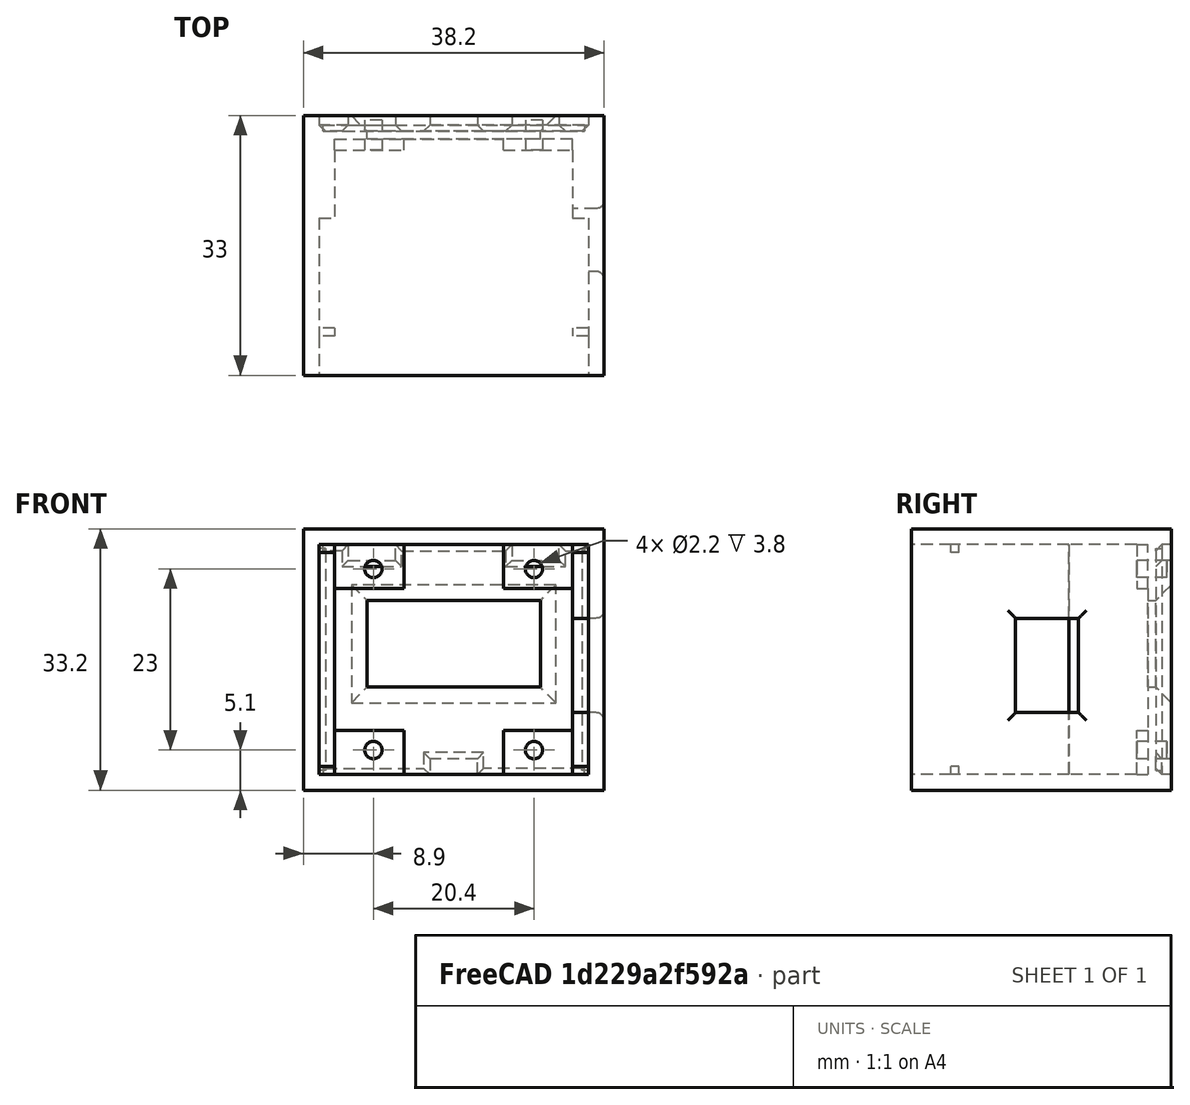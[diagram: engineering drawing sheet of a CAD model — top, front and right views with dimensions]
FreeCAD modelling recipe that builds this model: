
FCSTD DOCUMENT  (FreeCAD 1.2R20251216 (Git shallow))
Label: oled128x64_096-esp8266
License: All rights reserved
LicenseURL: https://en.wikipedia.org/wiki/All_rights_reserved
objects: Sketcher::SketchObject×9, PartDesign::Pad×6, PartDesign::Pocket×3, App::Point×2, PartDesign::Chamfer×2, PartDesign::Body×2, PartDesign::SubShapeBinder×1, PartDesign::Fillet×1
note: 57 computed .brp shape members not serialized (recipe doc carries the construction recipe); baked Part::Feature solids carry a one-line shape summary decoded from their .brp

FEATURE [App::Point] Origin001
  Role = Origin
FEATURE [Sketcher::SketchObject] Sketch  label="base"
  ArcFitTolerance = 1e-06
  AttachmentSupport = -> [Origin]
  ExternalTypes = [0]
  FullyConstrained = true
  MakeInternals = false
  MapMode = 5
  Placement = pos=(0,0,0) rot=(1,0,0;1.5708rad)
  sketch-geometry (5):
    g0: LineSegment StartX=-19.1 StartY=-16.6 StartZ=0 EndX=19.1 EndY=-16.6 EndZ=0
    g1: LineSegment StartX=19.1 StartY=-16.6 StartZ=0 EndX=19.1 EndY=16.6 EndZ=0
    g2: LineSegment StartX=19.1 StartY=16.6 StartZ=0 EndX=-19.1 EndY=16.6 EndZ=0
    g3: LineSegment StartX=-19.1 StartY=16.6 StartZ=0 EndX=-19.1 EndY=-16.6 EndZ=0
    g4: GeomPoint [constr] X=0 Y=0 Z=0
  constraints (12):
    c: Coincident(g0,g1)
    c: Coincident(g1,g2)
    c: Coincident(g2,g3)
    c: Coincident(g3,g0)
    c: Horizontal(g0)
    c: Horizontal(g2)
    c: Vertical(g1)
    c: Vertical(g3)
    c: Symmetric(g2,g0,g4)
    c: Distance(g1,g3) = 38.2
    c: Distance(g0,g2) = 33.2
    c: Coincident(g4,g-1)
FEATURE [PartDesign::Pad] Pad  label="base-pad"
  Direction = (0,-1,2e-16)
  Length = 3
  Length2 = 10
  Profile = -> Sketch
  ReferenceAxis = -> Sketch [N_Axis]
  Refine = true
  SideType = 0
  Suppressed = false
  Type = 0
  Type2 = 0
FEATURE [Sketcher::SketchObject] Sketch001  label="arduino-support-sketch"
  ArcFitTolerance = 1e-06
  AttachmentSupport = -> [Pad]
  ExternalGeometry = -> [Pad]
  ExternalTypes = [0,0,0,0]
  FullyConstrained = true
  MakeInternals = false
  MapMode = 5
  Placement = pos=(0,-3,0) rot=(1,0,0;1.5708rad)
  sketch-geometry (5):
    g0: LineSegment StartX=-15.1 StartY=-14.6 StartZ=0 EndX=15.1 EndY=-14.6 EndZ=0
    g1: LineSegment StartX=15.1 StartY=-14.6 StartZ=0 EndX=15.1 EndY=14.6 EndZ=0
    g2: LineSegment StartX=15.1 StartY=14.6 StartZ=0 EndX=-15.1 EndY=14.6 EndZ=0
    g3: LineSegment StartX=-15.1 StartY=14.6 StartZ=0 EndX=-15.1 EndY=-14.6 EndZ=0
    g4: GeomPoint [constr] X=0 Y=0 Z=0
  constraints (12):
    c: Coincident(g0,g1)
    c: Coincident(g1,g2)
    c: Coincident(g2,g3)
    c: Coincident(g3,g0)
    c: Horizontal(g0)
    c: Horizontal(g2)
    c: Vertical(g1)
    c: Vertical(g3)
    c: Symmetric(g2,g0,g4)
    c: Coincident(g4,g-1)
    c: DistanceY(g2,g-5) = 2
    c: DistanceX(g-4,g0) = 4
FEATURE [PartDesign::Pad] Pad001  label="arduino-support-pad"
  BaseFeature = -> Pad
  Direction = (0,-1,2e-16)
  Length = 10
  Length2 = 10
  Profile = -> Sketch001
  ReferenceAxis = -> Sketch001 [N_Axis]
  Refine = true
  SideType = 0
  Suppressed = false
  Type = 0
  Type2 = 0
FEATURE [Sketcher::SketchObject] Sketch002  label="sides-sketch"
  ArcFitTolerance = 1e-06
  AttachmentSupport = -> [Pad001]
  ExternalGeometry = -> [Pad001]
  ExternalTypes = [0,0,0,0,0]
  FullyConstrained = true
  MakeInternals = false
  MapMode = 5
  Placement = pos=(0,-13,0) rot=(1,0,0;1.5708rad)
  sketch-geometry (7):
    g0: LineSegment StartX=-17.1 StartY=-14.6 StartZ=0 EndX=17.1 EndY=-14.6 EndZ=0
    g1: LineSegment StartX=17.1 StartY=-14.6 StartZ=0 EndX=17.1 EndY=14.6 EndZ=0
    g2: LineSegment StartX=17.1 StartY=14.6 StartZ=0 EndX=-17.1 EndY=14.6 EndZ=0
    g3: LineSegment StartX=-17.1 StartY=14.6 StartZ=0 EndX=-17.1 EndY=-14.6 EndZ=0
    g4: GeomPoint [constr] X=0 Y=0 Z=0
    g5: LineSegment [constr] StartX=1.1e-15 StartY=16.6 StartZ=0 EndX=-2.4e-15 EndY=14.6 EndZ=0
    g6: LineSegment [constr] StartX=-19.1 StartY=1.8e-15 StartZ=0 EndX=-17.1 EndY=1.8e-15 EndZ=0
  constraints (17):
    c: Coincident(g0,g1)
    c: Coincident(g1,g2)
    c: Coincident(g2,g3)
    c: Coincident(g3,g0)
    c: Horizontal(g0)
    c: Horizontal(g2)
    c: Vertical(g1)
    c: Vertical(g3)
    c: Symmetric(g2,g0,g4)
    c: Coincident(g4,g-1)
    c: PointOnObject(g-7,g2)
    c: Symmetric(g-3,g-3,g5)
    c: Symmetric(g2,g2,g5)
    c: Symmetric(g-4,g-4,g6)
    c: Horizontal(g6)
    c: Equal(g5,g6)
    c: PointOnObject(g6,g3)
FEATURE [PartDesign::Pad] Pad002  label="sides-pad"
  BaseFeature = -> Pad001
  Direction = (0,-1,2e-16)
  Length = 20
  Length2 = 10
  Profile = -> Sketch002
  ReferenceAxis = -> Sketch002 [N_Axis]
  Refine = true
  SideType = 0
  Suppressed = false
  Type = 0
  Type2 = 0
FEATURE [Sketcher::SketchObject] Sketch003  label="display-support-sketch"
  ArcFitTolerance = 1e-06
  AttachmentSupport = -> [Pad]
  ExternalGeometry = -> [Sketch001]
  ExternalTypes = [0,0,0,0]
  FullyConstrained = true
  MakeInternals = false
  MapMode = 5
  Placement = pos=(0,-3,0) rot=(1,0,0;1.5708rad)
  sketch-geometry (27):
    g0: LineSegment [constr] StartX=-12.5 StartY=-13.7 StartZ=0 EndX=12.5 EndY=-13.7 EndZ=0
    g1: LineSegment [constr] StartX=12.5 StartY=-13.7 StartZ=0 EndX=12.5 EndY=13.7 EndZ=0
    g2: LineSegment [constr] StartX=12.5 StartY=13.7 StartZ=0 EndX=-12.5 EndY=13.7 EndZ=0
    g3: LineSegment [constr] StartX=-12.5 StartY=13.7 StartZ=0 EndX=-12.5 EndY=-13.7 EndZ=0
    g4: GeomPoint [constr] X=0 Y=0 Z=0
    g5: LineSegment StartX=6.3 StartY=14.6 StartZ=0 EndX=6.3 EndY=9 EndZ=0
    g6: LineSegment StartX=6.3 StartY=9 StartZ=0 EndX=15.1 EndY=9 EndZ=0
    g7: LineSegment StartX=15.1 StartY=9 StartZ=0 EndX=15.1 EndY=14.6 EndZ=0
    g8: LineSegment StartX=15.1 StartY=14.6 StartZ=0 EndX=6.3 EndY=14.6 EndZ=0
    g9: LineSegment [constr] StartX=-12.5 StartY=13.7 StartZ=0 EndX=-12.5 EndY=9 EndZ=0
    g10: LineSegment [constr] StartX=-6.3 StartY=13.7 StartZ=0 EndX=-12.5 EndY=13.7 EndZ=0
    g11: LineSegment StartX=6.3 StartY=-9 StartZ=0 EndX=6.3 EndY=-14.6 EndZ=0
    g12: LineSegment StartX=6.3 StartY=-14.6 StartZ=0 EndX=15.1 EndY=-14.6 EndZ=0
    g13: LineSegment StartX=15.1 StartY=-14.6 StartZ=0 EndX=15.1 EndY=-9 EndZ=0
    g14: LineSegment StartX=15.1 StartY=-9 StartZ=0 EndX=6.3 EndY=-9 EndZ=0
    g15: LineSegment StartX=-15.1 StartY=-9 StartZ=0 EndX=-15.1 EndY=-14.6 EndZ=0
    g16: LineSegment StartX=-15.1 StartY=-14.6 StartZ=0 EndX=-6.3 EndY=-14.6 EndZ=0
    g17: LineSegment StartX=-6.3 StartY=-14.6 StartZ=0 EndX=-6.3 EndY=-9 EndZ=0
    g18: LineSegment StartX=-6.3 StartY=-9 StartZ=0 EndX=-15.1 EndY=-9 EndZ=0
    g19: Circle CenterX=-10.2 CenterY=11.5 CenterZ=0 NormalX=0 NormalY=0 NormalZ=1 AngleXU=0 Radius=1.1
    g20: Circle CenterX=10.2 CenterY=11.5 CenterZ=0 NormalX=0 NormalY=0 NormalZ=1 AngleXU=0 Radius=1.1
    g21: Circle CenterX=10.2 CenterY=-11.5 CenterZ=0 NormalX=0 NormalY=0 NormalZ=1 AngleXU=0 Radius=1.1
    g22: Circle CenterX=-10.2 CenterY=-11.5 CenterZ=0 NormalX=0 NormalY=0 NormalZ=1 AngleXU=0 Radius=1.1
    g23: LineSegment StartX=-6.3 StartY=14.6 StartZ=0 EndX=-15.1 EndY=14.6 EndZ=0
    g24: LineSegment StartX=-15.1 StartY=14.6 StartZ=0 EndX=-15.1 EndY=9 EndZ=0
    g25: LineSegment StartX=-15.1 StartY=9 StartZ=0 EndX=-6.3 EndY=9 EndZ=0
    g26: LineSegment StartX=-6.3 StartY=14.6 StartZ=0 EndX=-6.3 EndY=9 EndZ=0
  constraints (72):
    c: Coincident(g1,g2)
    c: Coincident(g2,g3)
    c: Coincident(g3,g0)
    c: Horizontal(g0)
    c: Horizontal(g2)
    c: Vertical(g1)
    c: Vertical(g3)
    c: Symmetric(g2,g0,g4)
    c: Distance(g1,g3) = 25
    c: Distance(g0,g2) = 27.4
    c: Coincident(g4,g-1)
    c: Coincident(g5,g6)
    c: Coincident(g6,g7)
    c: Coincident(g7,g8)
    c: Coincident(g8,g5)
    c: Vertical(g5)
    c: Vertical(g7)
    c: Horizontal(g6)
    c: Horizontal(g8)
    c: Coincident(g10,g9)
    c: Vertical(g9)
    c: Horizontal(g10)
    c: Distance(g9,g10) = 6.2
    c: Distance(g9,g10) = 4.7
    c: Coincident(g11,g12)
    c: Coincident(g12,g13)
    c: Coincident(g13,g14)
    c: Coincident(g14,g11)
    c: Vertical(g11)
    c: Vertical(g13)
    c: Horizontal(g12)
    c: Horizontal(g14)
    c: Coincident(g15,g16)
    c: Coincident(g16,g17)
    c: Coincident(g17,g18)
    c: Coincident(g18,g15)
    c: Vertical(g15)
    c: Vertical(g17)
    c: Horizontal(g16)
    c: Horizontal(g18)
    c: Coincident(g9,g2)
    c: Diameter(g19) = 2.2
    c: DistanceX(g19,g20) = 20.4
    c: DistanceY(g21,g20) = 23
    c: Vertical(g20,g21)
    c: Horizontal(g21,g22)
    c: Symmetric(g19,g20,g-2)
    c: Symmetric(g19,g22,g-1)
    c: PointOnObject(g24,g-3)
    c: PointOnObject(g23,g-4)
    c: Coincident(g23,g-4)
    c: Coincident(g24,g23)
    c: Coincident(g25,g24)
    c: Horizontal(g25)
    c: PointOnObject(g9,g25)
    c: Coincident(g26,g23)
    c: Coincident(g26,g25)
    c: Vertical(g26)
    c: PointOnObject(g10,g26)
    c: Equal(g23,g18)
    c: Equal(g23,g14)
    c: Coincident(g15,g-3)
    c: Equal(g24,g11)
    c: Coincident(g12,g-6)
    c: Equal(g15,g24)
    c: Equal(g23,g8)
    c: Equal(g26,g5)
    c: Coincident(g7,g-6)
    c: Equal(g19,g22)
    c: Equal(g19,g21)
    c: Equal(g19,g20)
    c: Coincident(g0,g1)
FEATURE [PartDesign::Pad] Pad003  label="display-support-pad"
  BaseFeature = -> Pad002
  Direction = (0,-1,2e-16)
  Length = 1.4
  Length2 = 1
  Profile = -> Sketch003
  ReferenceAxis = -> Sketch003 [N_Axis]
  Refine = true
  SideType = 1
  Suppressed = false
  Type = 0
  Type2 = 0
FEATURE [Sketcher::SketchObject] Sketch004  label="display-hole-sketch"
  ArcFitTolerance = 1e-06
  AttachmentSupport = -> [Pad]
  ExternalTypes = [0]
  FullyConstrained = true
  MakeInternals = false
  MapMode = 5
  Placement = pos=(0,-3,0) rot=(1,0,0;1.5708rad)
  sketch-geometry (6):
    g0: LineSegment StartX=-11 StartY=-3.5 StartZ=0 EndX=11 EndY=-3.5 EndZ=0
    g1: LineSegment StartX=11 StartY=-3.5 StartZ=0 EndX=11 EndY=7.5 EndZ=0
    g2: LineSegment StartX=11 StartY=7.5 StartZ=0 EndX=-11 EndY=7.5 EndZ=0
    g3: LineSegment StartX=-11 StartY=7.5 StartZ=0 EndX=-11 EndY=-3.5 EndZ=0
    g4: GeomPoint [constr] X=0 Y=0 Z=0
    g5: GeomPoint [constr] X=0 Y=2 Z=0
  constraints (14):
    c: Coincident(g0,g1)
    c: Coincident(g1,g2)
    c: Coincident(g2,g3)
    c: Coincident(g3,g0)
    c: Horizontal(g0)
    c: Horizontal(g2)
    c: Vertical(g1)
    c: Vertical(g3)
    c: Distance(g1,g3) = 22
    c: Distance(g0,g2) = 11
    c: Coincident(g4,g-1)
    c: PointOnObject(g5,g-2)
    c: DistanceY(g4,g5) = 2
    c: Symmetric(g2,g0,g5)
FEATURE [PartDesign::Pocket] Pocket  label="display-hole"
  BaseFeature = -> Pad003
  Direction = (0,1,-2e-16)
  Length = 5
  Length2 = 5
  Profile = -> Sketch004
  ReferenceAxis = -> Sketch004 [N_Axis]
  Refine = true
  SideType = 0
  Suppressed = false
  Type = 2
  Type2 = 0
FEATURE [Sketcher::SketchObject] Sketch006  label="display-holes-sketch"
  ArcFitTolerance = 1e-06
  AttachmentSupport = -> [Pad]
  ExternalGeometry = -> [Sketch003]
  ExternalTypes = [0,0,0,0]
  FullyConstrained = true
  MakeInternals = false
  MapMode = 5
  Placement = pos=(0,-3,0) rot=(1,0,0;1.5708rad)
FEATURE [App::Point] Origin003
  Role = Origin
FEATURE [PartDesign::SubShapeBinder] Binder  label="sides-sketch-Binder"
  BindCopyOnChange = 0
  BindMode = 0
  ClaimChildren = false
  Context = -> Body001 [Binder.]
  Fuse = false
  MakeFace = true
  OffsetFill = false
  OffsetIntersection = false
  OffsetJoinType = 0
  OffsetOpenResult = false
  PartialLoad = false
  Refine = true
  Relative = true
  Support = -> [Body[Sketch002.]]
  _Version = 2
FEATURE [Sketcher::SketchObject] Sketch007  label="back-cover-sketch"
  ArcFitTolerance = 1e-06
  AttachmentSupport = -> [Origin002]
  ExternalGeometry = -> [Binder]
  ExternalTypes = [0,0,0,0]
  FullyConstrained = true
  MakeInternals = false
  MapMode = 5
  Placement = pos=(0,0,0) rot=(1,0,0;1.5708rad)
  sketch-geometry (30):
    g0: LineSegment StartX=-13.4 StartY=14.6 StartZ=0 EndX=-13.4 EndY=12.6 EndZ=0
    g1: LineSegment StartX=-13.4 StartY=12.6 StartZ=0 EndX=-7.4 EndY=12.6 EndZ=0
    g2: LineSegment StartX=-7.4 StartY=12.6 StartZ=0 EndX=-7.4 EndY=14.6 EndZ=0
    g3: LineSegment StartX=7.4 StartY=14.6 StartZ=0 EndX=7.4 EndY=12.6 EndZ=0
    g4: LineSegment StartX=7.4 StartY=12.6 StartZ=0 EndX=13.4 EndY=12.6 EndZ=0
    g5: LineSegment StartX=13.4 StartY=12.6 StartZ=0 EndX=13.4 EndY=14.6 EndZ=0
    g6: LineSegment StartX=-3 StartY=-12.6 StartZ=0 EndX=-3 EndY=-14.6 EndZ=0
    g7: LineSegment StartX=3 StartY=-14.6 StartZ=0 EndX=3 EndY=-12.6 EndZ=0
    g8: LineSegment StartX=3 StartY=-12.6 StartZ=0 EndX=-3 EndY=-12.6 EndZ=0
    g9: LineSegment [constr] StartX=-7.4 StartY=14.6 StartZ=0 EndX=0 EndY=14.6 EndZ=0
    g10: LineSegment StartX=-16.6 StartY=14.6 StartZ=0 EndX=-13.4 EndY=14.6 EndZ=0
    g11: LineSegment StartX=-7.4 StartY=14.6 StartZ=0 EndX=0 EndY=14.6 EndZ=0
    g12: LineSegment StartX=0 StartY=14.6 StartZ=0 EndX=7.4 EndY=14.6 EndZ=0
    g13: LineSegment StartX=13.4 StartY=14.6 StartZ=0 EndX=16.6 EndY=14.6 EndZ=0
    g14: LineSegment StartX=3 StartY=-14.6 StartZ=0 EndX=16.6 EndY=-14.6 EndZ=0
    g15: LineSegment StartX=-16.6 StartY=-14.6 StartZ=0 EndX=-3 EndY=-14.6 EndZ=0
    g16: LineSegment [constr] StartX=-7.4 StartY=12.6 StartZ=0 EndX=-3.7 EndY=12.6 EndZ=0
    g17: LineSegment [constr] StartX=-3.7 StartY=12.6 StartZ=0 EndX=0 EndY=12.6 EndZ=0
    g18: LineSegment [constr] StartX=-13.4 StartY=12.6 StartZ=0 EndX=-17.1 EndY=12.6 EndZ=0
    g19: LineSegment StartX=-17.1 StartY=14.1 StartZ=0 EndX=-17.1 EndY=12.6 EndZ=0
    g20: LineSegment StartX=-17.1 StartY=12.6 StartZ=0 EndX=-17.1 EndY=-14.1 EndZ=0
    g21: LineSegment StartX=17.1 StartY=14.1 StartZ=0 EndX=17.1 EndY=-14.1 EndZ=0
    g22: ArcOfCircle CenterX=-16.6 CenterY=14.1 CenterZ=0 NormalX=0 NormalY=0 NormalZ=1 AngleXU=0 Radius=0.5 StartAngle=1.5708 EndAngle=3.14159
    g23: GeomPoint [constr] X=-17.1 Y=14.6 Z=0
    g24: ArcOfCircle CenterX=16.6 CenterY=14.1 CenterZ=0 NormalX=0 NormalY=0 NormalZ=1 AngleXU=0 Radius=0.5 StartAngle=-9e-16 EndAngle=1.5708
    g25: GeomPoint [constr] X=17.1 Y=14.6 Z=0
    g26: ArcOfCircle CenterX=16.6 CenterY=-14.1 CenterZ=0 NormalX=0 NormalY=0 NormalZ=1 AngleXU=0 Radius=0.5 StartAngle=4.71239 EndAngle=6.28319
    g27: GeomPoint [constr] X=17.1 Y=-14.6 Z=0
    g28: ArcOfCircle CenterX=-16.6 CenterY=-14.1 CenterZ=0 NormalX=0 NormalY=0 NormalZ=1 AngleXU=0 Radius=0.5 StartAngle=3.14159 EndAngle=4.71239
    g29: GeomPoint [constr] X=-17.1 Y=-14.6 Z=0
  constraints (74):
    c: Coincident(g0,g1)
    c: Coincident(g1,g2)
    c: Vertical(g0)
    c: Vertical(g2)
    c: Horizontal(g1)
    c: Distance(g0,g2) = 6
    c: Distance(g1,g0) = 2
    c: Coincident(g3,g4)
    c: Coincident(g4,g5)
    c: Vertical(g3)
    c: Vertical(g5)
    c: Horizontal(g4)
    c: Coincident(g7,g8)
    c: Coincident(g8,g6)
    c: Vertical(g6)
    c: Vertical(g7)
    c: Coincident(g9,g2)
    c: Symmetric(g6,g7,g-2)
    c: Equal(g0,g3)
    c: Equal(g0,g6)
    c: Equal(g1,g4)
    c: Equal(g1,g8)
    c: Coincident(g10,g0)
    c: Coincident(g11,g2)
    c: Coincident(g11,g9)
    c: Horizontal(g11)
    c: Coincident(g12,g9)
    c: Coincident(g12,g3)
    c: Coincident(g13,g5)
    c: Horizontal(g13)
    c: Coincident(g14,g7)
    c: Horizontal(g14)
    c: Coincident(g15,g6)
    c: Horizontal(g15)
    c: Symmetric(g2,g3,g9)
    c: PointOnObject(g9,g-2)
    c: Coincident(g16,g1)
    c: Horizontal(g16)
    c: Coincident(g17,g16)
    c: Horizontal(g17)
    c: Coincident(g18,g0)
    c: Horizontal(g18)
    c: Equal(g18,g16)
    c: Equal(g16,g17)
    c: PointOnObject(g17,g-2)
    c: Horizontal(g0,g2)
    c: Coincident(g19,g18)
    c: Vertical(g19)
    c: Coincident(g20,g18)
    c: Vertical(g20)
    c: Equal(g7,g6)
    c: Coincident(g-3,g23)
    c: PointOnObject(g23,g19)
    c: PointOnObject(g23,g10)
    c: Tangent(g19,g22) = -1.5708
    c: Tangent(g10,g22) = 1.5708
    c: PointOnObject(g25,g13)
    c: PointOnObject(g25,g21)
    c: Tangent(g13,g24) = 1.5708
    c: Tangent(g21,g24) = 1.5708
    c: PointOnObject(g27,g21)
    c: PointOnObject(g27,g14)
    c: Tangent(g21,g26) = 1.5708
    c: Tangent(g14,g26) = -1.5708
    c: Tangent(g20,g28) = -1.5708
    c: Tangent(g15,g28) = -1.5708
    c: Equal(g22,g24)
    c: Equal(g24,g26)
    c: Equal(g26,g28)
    c: Radius(g22) = 0.5
    c: Horizontal(g23,g10)
    c: Coincident(g29,g-4)
    c: Coincident(g27,g-5)
    c: Coincident(g25,g-6)
FEATURE [PartDesign::Pad] Pad004  label="back-cover-pad"
  Direction = (0,-1,2e-16)
  Length = 2
  Length2 = 10
  Profile = -> Sketch007
  ReferenceAxis = -> Sketch007 [N_Axis]
  Refine = true
  SideType = 0
  Suppressed = false
  Type = 0
  Type2 = 0
FEATURE [PartDesign::Chamfer] Chamfer001  label="back-cover-pad-chamfer"
  Angle = 45
  Base = -> Pad004 [Edge60,Edge4,Edge7,Edge10,Edge13,Edge59,Edge34,Edge36,Edge38,Edge40,Edge44,Edge48,Edge50,Edge52,Edge54,Edge56,Edge58,Edge46,Edge16,Edge42]
  BaseFeature = -> Pad004
  ChamferType = 0
  FlipDirection = false
  Refine = true
  Size = 0.8
  Size2 = 1
  SupportTransform = false
  Suppressed = false
  UseAllEdges = false
FEATURE [PartDesign::Body] Body001  label="back-cover"
  AllowCompound = false
  Group = -> [Sketch007,Binder,Pad004,Chamfer001]
  Origin = -> Origin002
  Tip = -> Chamfer001
FEATURE [PartDesign::Body] Body  label="face"
  AllowCompound = true
  Group = -> [Sketch,Pad,Sketch006,Sketch001,Pad001,Sketch002,Pad002,Sketch003,Pad003,Sketch004,Pocket,Sketch005,Pocket001,Fillet001,Pocket002,Chamfer,Sketch008,Pad005]
  Origin = -> Origin
  Tip = -> Pad005
FEATURE [Sketcher::SketchObject] Sketch005  label="usb-hole-sketch"
  ArcFitTolerance = 1e-06
  AttachmentSupport = -> [Pocket002]
  ExternalGeometry = -> [Pad001]
  ExternalTypes = [0]
  FullyConstrained = true
  MakeInternals = false
  MapMode = 5
  Placement = pos=(19.1,0,0) rot=(0.57735,-0.57735,-0.57735;2.0944rad)
  sketch-geometry (7):
    g0: LineSegment StartX=11.8 StartY=-6.75 StartZ=0 EndX=19.8 EndY=-6.75 EndZ=0
    g1: LineSegment StartX=19.8 StartY=5.25 StartZ=0 EndX=11.8 EndY=5.25 EndZ=0
    g2: LineSegment StartX=11.8 StartY=5.25 StartZ=0 EndX=11.8 EndY=-6.75 EndZ=0
    g3: GeomPoint [constr] X=11.8 Y=-0.75 Z=0
    g4: GeomPoint [constr] X=11.8 Y=0 Z=0
    g5: LineSegment [constr] StartX=19.8 StartY=16.6 StartZ=0 EndX=19.8 EndY=-16.6 EndZ=0
    g6: LineSegment StartX=19.8 StartY=5.25 StartZ=0 EndX=19.8 EndY=-6.75 EndZ=0
  constraints (19):
    c: Coincident(g1,g2)
    c: Coincident(g2,g0)
    c: Horizontal(g0)
    c: Horizontal(g1)
    c: Vertical(g2)
    c: Distance(g0,g2) = 8
    c: Distance(g0,g1) = 12
    c: Symmetric(g2,g2,g3)
    c: PointOnObject(g4,g-1)
    c: PointOnObject(g4,g2)
    c: DistanceY(g3,g4) = 0.75
    c: Vertical(g5)
    c: Horizontal(g-3,g5)
    c: Horizontal(g-3,g5)
    c: PointOnObject(g0,g5)
    c: PointOnObject(g1,g5)
    c: Coincident(g6,g1)
    c: Coincident(g6,g0)
    c: DistanceX(g1,g-3) = 1.2
FEATURE [PartDesign::Pocket] Pocket001  label="usb-hole-pocket"
  BaseFeature = -> Pocket
  Direction = (1,0,0)
  Length = 5
  Length2 = 5
  Profile = -> Sketch005
  ReferenceAxis = -> Sketch005 [N_Axis]
  Refine = true
  Reversed = true
  SideType = 0
  Suppressed = false
  Type = 0
  Type2 = 0
FEATURE [PartDesign::Fillet] Fillet001  label="usb-hole-fillet"
  Base = -> Pocket001 [Edge16,Edge17,Edge18,Edge19]
  BaseFeature = -> Pocket001
  Radius = 1
  Refine = true
  SupportTransform = false
  Suppressed = false
  UseAllEdges = false
FEATURE [PartDesign::Pocket] Pocket002  label="display-holes-pocket"
  BaseFeature = -> Fillet001
  Direction = (0,1,-2e-16)
  Length = 2.4
  Length2 = 5
  Profile = -> Sketch006
  ReferenceAxis = -> Sketch006 [N_Axis]
  Refine = true
  SideType = 0
  Suppressed = false
  Type = 0
  Type2 = 0
FEATURE [PartDesign::Chamfer] Chamfer  label="chamfer"
  Angle = 45
  Base = -> Pocket002 [Edge35,Edge34,Edge37,Edge36]
  BaseFeature = -> Pocket002
  ChamferType = 0
  FlipDirection = false
  Refine = true
  Size = 2
  Size2 = 1
  SupportTransform = false
  Suppressed = false
  UseAllEdges = false
FEATURE [Sketcher::SketchObject] Sketch008  label="back-cover-blockers-sketch"
  ArcFitTolerance = 1e-06
  AttachmentOffset = pos=(0,0,-6) rot=(0,0,1;0rad)
  AttachmentSupport = -> [Chamfer]
  ExternalGeometry = -> [Chamfer]
  ExternalTypes = [0,0,0,0]
  FullyConstrained = true
  MakeInternals = false
  MapMode = 5
  Placement = pos=(0,-27,6.3e-15) rot=(1,0,0;1.5708rad)
  sketch-geometry (16):
    g0: LineSegment StartX=-17.1 StartY=14.6 StartZ=0 EndX=-17.1 EndY=13.6 EndZ=0
    g1: LineSegment StartX=-17.1 StartY=13.6 StartZ=0 EndX=-15.1 EndY=13.6 EndZ=0
    g2: LineSegment StartX=-15.1 StartY=13.6 StartZ=0 EndX=-15.1 EndY=14.6 EndZ=0
    g3: LineSegment StartX=-15.1 StartY=14.6 StartZ=0 EndX=-17.1 EndY=14.6 EndZ=0
    g4: LineSegment StartX=15.1 StartY=14.6 StartZ=0 EndX=15.1 EndY=13.6 EndZ=0
    g5: LineSegment StartX=15.1 StartY=13.6 StartZ=0 EndX=17.1 EndY=13.6 EndZ=0
    g6: LineSegment StartX=17.1 StartY=13.6 StartZ=0 EndX=17.1 EndY=14.6 EndZ=0
    g7: LineSegment StartX=17.1 StartY=14.6 StartZ=0 EndX=15.1 EndY=14.6 EndZ=0
    g8: LineSegment StartX=15.1 StartY=-14.6 StartZ=0 EndX=15.1 EndY=-13.6 EndZ=0
    g9: LineSegment StartX=17.1 StartY=-14.6 StartZ=0 EndX=15.1 EndY=-14.6 EndZ=0
    g10: LineSegment StartX=-17.1 StartY=-14.6 StartZ=0 EndX=-17.1 EndY=-13.6 EndZ=0
    g11: LineSegment StartX=-17.1 StartY=-13.6 StartZ=0 EndX=-15.1 EndY=-13.6 EndZ=0
    g12: LineSegment StartX=-15.1 StartY=-13.6 StartZ=0 EndX=-15.1 EndY=-14.6 EndZ=0
    g13: LineSegment StartX=-15.1 StartY=-14.6 StartZ=0 EndX=-17.1 EndY=-14.6 EndZ=0
    g14: LineSegment StartX=15.1 StartY=-13.6 StartZ=0 EndX=17.1 EndY=-13.6 EndZ=0
    g15: LineSegment StartX=17.1 StartY=-14.6 StartZ=0 EndX=17.1 EndY=-13.6 EndZ=0
  constraints (44):
    c: Coincident(g0,g1)
    c: Coincident(g1,g2)
    c: Coincident(g2,g3)
    c: Coincident(g3,g0)
    c: Vertical(g0)
    c: Vertical(g2)
    c: Horizontal(g1)
    c: Horizontal(g3)
    c: Distance(g0,g2) = 2
    c: Distance(g1,g3) = 1
    c: Coincident(g-3,g0)
    c: Coincident(g4,g5)
    c: Coincident(g5,g6)
    c: Coincident(g6,g7)
    c: Coincident(g7,g4)
    c: Vertical(g4)
    c: Vertical(g6)
    c: Horizontal(g5)
    c: Horizontal(g7)
    c: Equal(g2,g6)
    c: Equal(g3,g7)
    c: Coincident(g6,g-6)
    c: Equal(g3,g13)
    c: Equal(g3,g9)
    c: Equal(g0,g10)
    c: Equal(g0,g8)
    c: Vertical(g8)
    c: Vertical(g15)
    c: Horizontal(g9)
    c: Horizontal(g14)
    c: Horizontal(g13)
    c: Horizontal(g11)
    c: Vertical(g10)
    c: Vertical(g12)
    c: Coincident(g13,g10)
    c: Coincident(g10,g11)
    c: Coincident(g12,g11)
    c: Coincident(g12,g13)
    c: Coincident(g8,g9)
    c: Coincident(g8,g14)
    c: Coincident(g14,g15)
    c: Coincident(g9,g15)
    c: Coincident(g-5,g9)
    c: Coincident(g10,g-4)
FEATURE [PartDesign::Pad] Pad005  label="back-cover-blockers-pad"
  BaseFeature = -> Chamfer
  Direction = (0,-1,2e-16)
  Length = 1
  Length2 = 10
  Profile = -> Sketch008
  ReferenceAxis = -> Sketch008 [N_Axis]
  Refine = true
  SideType = 0
  Suppressed = false
  Type = 0
  Type2 = 0
